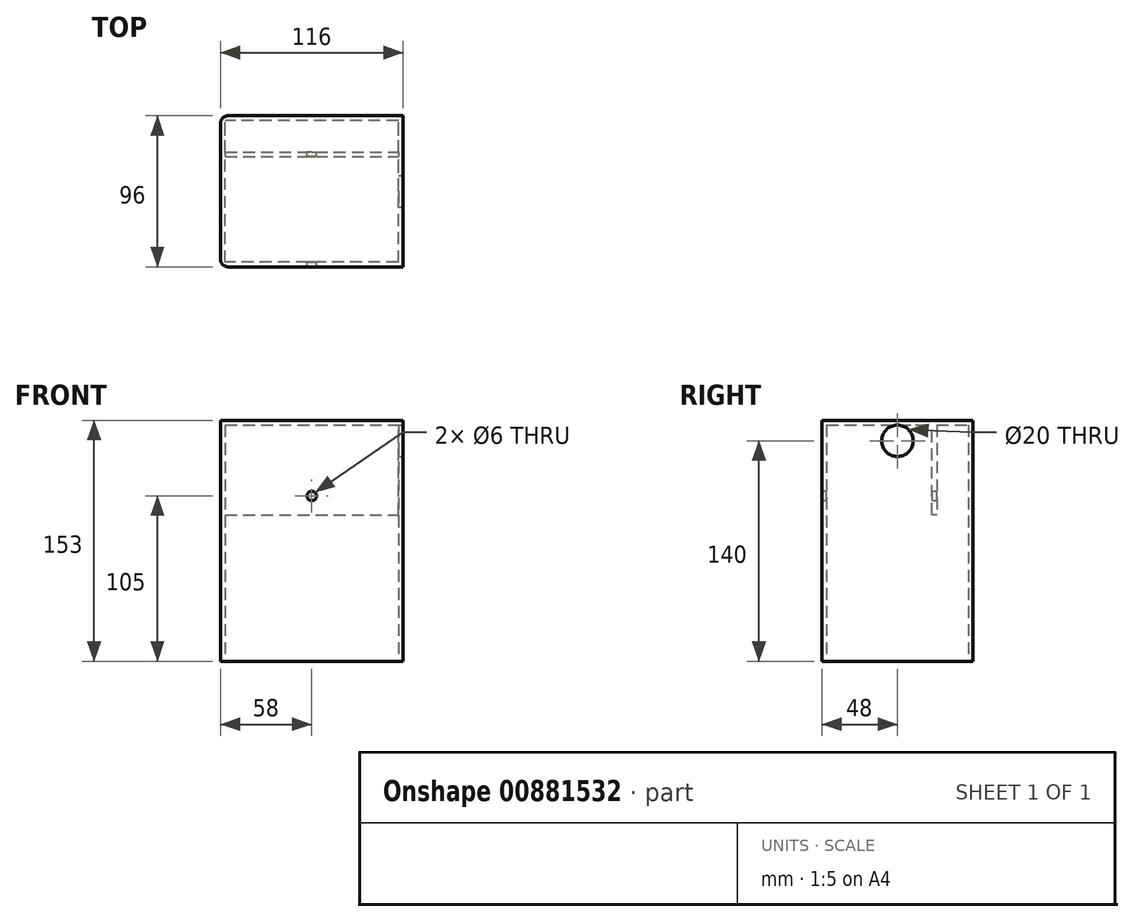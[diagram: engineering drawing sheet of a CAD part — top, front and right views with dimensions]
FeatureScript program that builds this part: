
annotation { "Feature Type Name" : "Feature", "Feature Type Description" : "" }
export const myFeature = defineFeature(function(context is Context, id is Id, definition is map)
    precondition{}
    {
        {
            var Q0;
            Q0=qCreatedBy(makeId("Top.planeOp"),FACE);
            var sketch = newSketch(context, id + "F0", { "sketchPlane" : qUnion([Q0])});
            skLineSegment(sketch, "E0.bottom", {"start": v(55, -45) * mm, "end": v(-55, -45) * mm});
            skLineSegment(sketch, "E0.top", {"start": v(55, 45) * mm, "end": v(-55, 45) * mm});
            skLineSegment(sketch, "E0.left", {"start": v(55, -45) * mm, "end": v(55, 45) * mm});
            skLineSegment(sketch, "E0.right", {"start": v(-55, -45) * mm, "end": v(-55, 45) * mm});
            skPoint(sketch, "E0.middle", {"position": v(0, 0) * mm});
            skSolve(sketch);
        }
        {
            var Q0;
            Q0=qSketchRegion(id+"F0",true);
            extrude(context, id + "F1", {"entities" : qUnion([Q0]), "depth" : 150 * mm, "offsetDistance" : 25.4 * mm, "symmetric" : true});
        }
        {
            var Q0;
            Q0=makeQuery(id+"F1.opExtrude","CAP_FACE",FACE,{"disambiguationData":[OSD([sQuery(id+"F0.wireOp",EDGE,"E0.bottom"),sQuery(id+"F0.wireOp",EDGE,"E0.top"),sQuery(id+"F0.wireOp",EDGE,"E0.left"),sQuery(id+"F0.wireOp",EDGE,"E0.right")])],"isStart":true});
            shell(context, id + "F2", {"entities" : qUnion([Q0]), "thickness" : 3 * mm, "oppositeDirection" : true});
        }
        {
            var Q0;
            Q0=makeQuery(id+"F1.opExtrude","SWEPT_FACE",FACE,{"disambiguationData":[OSD([sQuery(id+"F0.wireOp",EDGE,"E0.left")])]});
            var sketch = newSketch(context, id + "F3", { "sketchPlane" : qUnion([Q0])});
            skLineSegment(sketch, "E1.left", {"start": v(35, -35) * mm, "end": v(35, -34.97) * mm});
            skPoint(sketch, "E1.middle", {"position": v(0, 0) * mm});
            skLineSegment(sketch, "E2.trimOffspring", {"start": v(35, 34.97) * mm, "end": v(35, 35) * mm});
            skLineSegment(sketch, "E3", {"start": v(35, 35) * mm, "end": v(35, 34.97) * mm});
            skLineSegment(sketch, "E4.0.0", {"start": v(-48, -75) * mm, "end": v(48, -75) * mm});
            skLineSegment(sketch, "E4.0.1", {"start": v(48, -75) * mm, "end": v(48, 78) * mm});
            skLineSegment(sketch, "E4.0.2", {"start": v(48, 78) * mm, "end": v(-48, 78) * mm});
            skLineSegment(sketch, "E4.0.3", {"start": v(-48, 78) * mm, "end": v(-48, -75) * mm});
            skLineSegment(sketch, "E5", {"start": v(0, 78) * mm, "end": v(0, 75) * mm});
            skLineSegment(sketch, "E6", {"start": v(0, 75) * mm, "end": v(-10, 75) * mm});
            skLineSegment(sketch, "E7", {"start": v(-10, 75) * mm, "end": v(-10, 55) * mm});
            skLineSegment(sketch, "E8", {"start": v(-10, 55) * mm, "end": v(10, 55) * mm});
            skLineSegment(sketch, "E9", {"start": v(10, 55) * mm, "end": v(10, 75) * mm});
            skLineSegment(sketch, "E10", {"start": v(0, 75) * mm, "end": v(0, 55) * mm});
            skCircle(sketch, "E11", {"center": v(0, 65) * mm, "radius": 10 * mm});
            skLineSegment(sketch, "E12", {"start": v(0, 75) * mm, "end": v(10, 75) * mm});
            skSolve(sketch);
        }
        {
            var Q0;
            {var subQ0=sQuery(id+"F3.wireOp",EDGE,"E10");Q0=makeQuery(id+"F3.imprint","IMPRINT",FACE,{"disambiguationData":[TD([[makeQuery(id+"F3.imprint","IMPRINT",EDGE,{"derivedFrom":subQ0}),-1.0]])]});}
            var Q1;
            {var subQ0=sQuery(id+"F3.wireOp",EDGE,"E10");Q1=makeQuery(id+"F3.imprint","IMPRINT",FACE,{"disambiguationData":[TD([[makeQuery(id+"F3.imprint","IMPRINT",EDGE,{"derivedFrom":subQ0}),1.0]])]});}
            extrude(context, id + "F4", {"entities" : qUnion([Q0, Q1]), "operationType" : NewBodyOperationType.REMOVE, "oppositeDirection" : true, "depth" : 25.4 * mm, "offsetDistance" : 25.4 * mm});
        }
        {
            var Q0;
            Q0=makeQuery(id+"F2.opShell","OFFSET_FACE",FACE,{"disambiguationData":[OSD([sQuery(id+"F0.wireOp",EDGE,"E0.left")])]});
            var sketch = newSketch(context, id + "F5", { "sketchPlane" : qUnion([Q0])});
            skLineSegment(sketch, "E13.0.0", {"start": v(-48, -75) * mm, "end": v(48, -75) * mm});
            skLineSegment(sketch, "E13.0.1", {"start": v(48, -75) * mm, "end": v(48, 78) * mm});
            skLineSegment(sketch, "E13.0.2", {"start": v(48, 78) * mm, "end": v(-48, 78) * mm});
            skLineSegment(sketch, "E13.0.3", {"start": v(-48, 78) * mm, "end": v(-48, -75) * mm});
            skLineSegment(sketch, "E14", {"start": v(0, 78) * mm, "end": v(0, 0) * mm, "construction": true});
            skLineSegment(sketch, "E15", {"start": v(-48, 78) * mm, "end": v(-45, 78) * mm, "construction": true});
            skLineSegment(sketch, "E16", {"start": v(-45, 78) * mm, "end": v(-25, 78) * mm, "construction": true});
            skLineSegment(sketch, "E17", {"start": v(-25, 78) * mm, "end": v(-25, 18) * mm});
            skLineSegment(sketch, "E18", {"start": v(-25, 18) * mm, "end": v(-22, 18) * mm, "construction": true});
            skLineSegment(sketch, "E19", {"start": v(-22, 18) * mm, "end": v(-22, 78) * mm});
            skLineSegment(sketch, "E20", {"start": v(-25, 18) * mm, "end": v(-22, 18) * mm});
            skSolve(sketch);
        }
        {
            var Q0;
            {var subQ0=sQuery(id+"F5.wireOp",EDGE,"E20");Q0=makeQuery(id+"F5.imprint","IMPRINT",FACE,{"disambiguationData":[TD([[makeQuery(id+"F5.imprint","IMPRINT",EDGE,{"derivedFrom":subQ0}),1.0]])]});}
            extrude(context, id + "F6", {"entities" : qUnion([Q0]), "operationType" : NewBodyOperationType.ADD, "depth" : 110 * mm, "offsetDistance" : 25 * mm});
        }
        {
            var Q0;
            Q0=makeQuery(id+"F2.opShell","OFFSET_FACE",FACE,{"disambiguationData":[OSD([sQuery(id+"F0.wireOp",EDGE,"E0.bottom")])]});
            var sketch = newSketch(context, id + "F7", { "sketchPlane" : qUnion([Q0])});
            skLineSegment(sketch, "E21.0.0", {"start": v(-58, -75) * mm, "end": v(58, -75) * mm});
            skLineSegment(sketch, "E21.0.1", {"start": v(58, -75) * mm, "end": v(58, 78) * mm});
            skLineSegment(sketch, "E21.0.2", {"start": v(58, 78) * mm, "end": v(-58, 78) * mm});
            skLineSegment(sketch, "E21.0.3", {"start": v(-58, 78) * mm, "end": v(-58, -75) * mm});
            skLineSegment(sketch, "E22", {"start": v(0, -75) * mm, "end": v(0, 30) * mm});
            skCircle(sketch, "E23", {"center": v(0, 30) * mm, "radius": 3 * mm});
            skSolve(sketch);
        }
        {
            var Q0;
            Q0=makeQuery(id+"F7.imprint","IMPRINT",FACE,{"disambiguationData":[TD([[makeQuery(id+"F7.imprint","IMPRINT",EDGE,{"derivedFrom":sQuery(id+"F7.wireOp",EDGE,"E23")}),1.0]])]});
            extrude(context, id + "F8", {"entities" : qUnion([Q0]), "operationType" : NewBodyOperationType.REMOVE, "oppositeDirection" : true, "depth" : 76 * mm, "offsetDistance" : 25.4 * mm, "hasSecondDirection" : true, "secondDirectionOppositeDirection" : false, "secondDirectionDepth" : 88 * mm});
        }
        {
            var Q0;
            Q0=makeQuery(id+"F1.opExtrude","SWEPT_EDGE",EDGE,{"disambiguationData":[OSD([sQuery(id+"F0.wireOp",EDGE,"E0.bottom"),sQuery(id+"F0.wireOp",EDGE,"E0.right")])]});
            var Q1;
            Q1=makeQuery(id+"F1.opExtrude","SWEPT_EDGE",EDGE,{"disambiguationData":[OSD([sQuery(id+"F0.wireOp",EDGE,"E0.top"),sQuery(id+"F0.wireOp",EDGE,"E0.right")])]});
            fillet(context, id + "F9", {"entities" : qUnion([Q0, Q1]), "radius" : 5 * mm, "tangentPropagation" : true, "allowEdgeOverflow" : false});
        }
    });
